# Revit family: Domotics-DomesticRanges-GEWISS-CHORUS_COMMAND-TWO-WAY_SWITCH_FAST_WIRING_2M
name_source: partatom
category: Apparecchi elettrici
revit_build: Autodesk Revit 2016 (Build: 20161004_0715(x64)
units: mm (PartAtom-declared; Revit-internal decimal feet)

## family parameters
Condiviso = Sì
Host = Superficie
Mantenere orientamento annotazione = Sì
Numero OmniClass = 23.80.50.11.14
Punto di calcolo locali = Sì
Quota connettore circolare = Usa diametro
Taglio con vuoti quando caricato = No
Tipo di parte = Normale
Titolo OmniClass = Switches

## types (9) — shared parameters
Bidimensionale = bidimensionale deviatori 2m : GW12073
Breaking capacity = 1.25 In (200 position changes)
Breaking capacity: = 1.25 In (200 position changes)
Carico apparente = 0 VA
Catalogue = DOMOTICS
Catalogue Range = CHORUS - DOMESTIC RANGE
Category = Two-way switch
Electrocod = 0130
Glow Wire Test = 850°C
IDF = feffdcad-0838-4101-afce-8ea840a0069e
IDT = 59cacd09-26dc-4fb2-a882-50e5d5bb77b0
Immagine tipo = GW14073.jpg
Insulation resistance = > 5 MOhm
Larghezza pulsante = 46 mm  [stored 0.150919 ft]
N poli = 1
No. Chorus modules = 2
Produttore = GEWISS S.p.A.
Prolonged operation (no.of position changes) = 40.000 at In 250 V ac cosÃ˜=0,6
Prospetto di default = 1219 mm
Resistance at test voltage = 2000 V at 50 Hz for 1 minute
SEO = 2 way switch
Simbolo = SIMBOLO DEVIATORI : DEV1PLUM
Standard = EN 60669-1
Standard; = EN 60669-1
Technical sheet = https://www.gewiss.com
Terminal grip on cable traction = > 50 N
Terminal tightening capacity = min. 0,75 - max. 2x4
Terminal tightening capacity flexible cables (mm2) = min. 0,75 - max. 2x4
Terminal tightening capacity rigid cables (mm2) = min. 0,5 - max. 2x2,5
Thermo-pressure with ball = 125
Tipo_ = CHORUS DEVIATORI 2M_BASE : GW14073 - Titanio - Illuminabile segnalazione
URL = https://www.gewiss.com
Version file RFA = 19.0
Volt = 230 V
Voltage = 250 V ac
Voltage: = 250 V ac
Wiring terminals = Quick, with spring

## per-type parameters (varying)
| type | Button key | Colour | Description: | Descrizione | EAN code | Modello | Type |
| GW14073F - 2-way switch 2M 1P 16AX ill sig fast wiring titanium | With replaceable neutral lens | Titanium | 1P - 16AX illuminable | 2-WAY SWITCH 2M 1P 16AX ILL SIG R.W. T | 8011564265646 | GW14073F | Indicator |
| GW10073F - 2-way switch, 2M 1P 16AX ill sig fast wiring white | With replaceable neutral lens | White | 1P - 16AX illuminable | 2-WAY SWITCH, 2M 1P 16AX ILL SIG R.W. W | 8011564258914 | GW10073F | Indicator |
| GW14072F - 2-way switch 2M 1P 16AX ill loc fast wiring titanium | With diffuser | Titanium | 1P - 16AX illuminable | 2-WAY SWITCH 2M 1P 16AX ILL LOC R.W. T | 8011564265622 | GW14072F | Backlit |
| GW14071F - 2-way switch 2M 1P 16AX fast wiring titanium | Neutral | Titanium | 1P - 16AX | 2-WAY SWITCH 2M 1P 16AX R.W. TITANIUM | 8011564265608 | GW14071F | General |
| GW12072F - 2-way switch, 2M 1P 16AX ill loc fast wiring black | With diffuser | Black | 1P - 16AX illuminable | 2-WAY SWITCH, 2M 1P 16AX ILL LOC R.W. B | 8011564269873 | GW12072F | Backlit |
| GW10072F - 2-way switch, 2M 1P 16AX ill loc fast wiring white | With diffuser | White | 1P - 16AX illuminable | 2-WAY SWITCH, 2M 1P 16AX ILL LOC R.W. W | 8011564257399 | GW10072F | Backlit |
| GW10071F - 2-way switch, 2M 1P 16AX fast wiring vhite | Neutral | White | 1P - 16AX | 2-WAY SWITCH, 2M 1P 16AX R.W. WHITE | 8011564257375 | GW10071F | General |
| GW12071F - 2-way switch, 2M 1P 16AX fast wiring black | Neutral | Black | 1P - 16AX | 2-WAY SWITCH, 2M 1P 16AX R.WIRING BLACK | 8011564269866 | GW12071F | General |
| GW12073F - 2-way switch, 2M 1P 16AX ill sig fast wiring black | With replaceable neutral lens | Black | 1P - 16AX illuminable | 2-WAY SWITCH, 2M 1P 16AX ILL SIG R.W. B | 8011564269880 | GW12073F | Indicator |

note: source unit labels omitted for Thermo-pressure with ball — the stored unit's dimension contradicts the parameter name (converter mislabeling)

note: [stored X ft] marks values corroborated as IEEE doubles in the binary element streams (Revit-internal decimal feet)

## geometry (parser evidence)
native form markers: Sweep x1
no freeform markers — native parametric forms only
